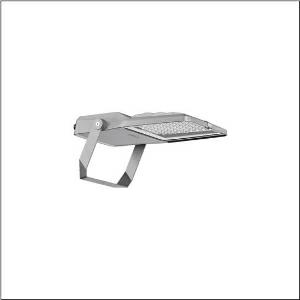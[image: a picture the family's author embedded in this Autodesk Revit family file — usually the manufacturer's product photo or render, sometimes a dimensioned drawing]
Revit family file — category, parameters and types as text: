
# Revit family: floodlight_fl_21_mini___pl64_5xa7772c2e1a_4ebe
name_source: partatom
category: Lighting Fixtures
units: mm (PartAtom-declared; Revit-internal decimal feet)

## family parameters
Cut with Voids When Loaded = No
Host = Face
Light Source = No
Part Type = Normal
Room Calculation Point = No
Round Connector Dimension = Use Diameter
Shared = No

## types (1)
- --- (1 x LED, 11790 lm, 87.2 W, 3000K)
    Apparent Load = 87 VA
    CIE Flux Codes = 28 80 98 100 100
    Color Rendering = 70
    Color Temperature = 3000K
    Default Elevation = 1800 mm
    Description = Floodlight FL 21 mini, floodlight, primary light control with lens, of PMMA, primary optical cover: protective disc, of toughened safety glass, transparent, light distribution: PL64, light emission: direct distribution, installation type: surface-mounted, LED, High Power LED, rated luminous flux: 11.790lm, luminous efficacy: 135lm/W, light colour: 730, colour temperature: 3000K, control gear: ECG iQ, control: Street-Remote, Auto-Match, Temp-Guard, Night-Set, Smart-Wire, Desk-Remote (wireless, voltage-free reading and setting of iQ features in the workshop via application-optimized NFC function/RFID function), optimised constant luminous flux control (CLO 2.0), with terminal, 6-pole, mains connection: 220..240V, AC, 50/60Hz, start of lifetime: 87W, end of lifetime: 92W, reduction: 40W, luminaire housing, of diecast aluminium, powder-coated, Siteco® metallic grey (DB 702S), corrosivity category C5 according to DIN EN ISO 12944, mounting bracket, of steel, galvanised, powder-coated, Siteco® metallic grey (DB 702S), protection rating (complete): IP66, insulation class (complete): insulation class II (safety insulation), certification: CE, ENEC, VDE, protection symbol: D, impact resistance: IK08, permissible operating ambient temperature: -40..+40°C, permissible operating ambient temperature for outdoor applications: -40..+50°C, standard: DIN EN 12944, packaging unit: 1 piece

Light Distribution: PL64
    Height = 70 mm
    Lamp = 1 x LED
    Lamp Light Flux = 11790 lm
    Lamp Power = 87.2 W
    Lamp count = 1
    Length = 485 mm
    Luminous efficacy = 135 lm/W
    Manufacturer = Siteco
    ModVariant = No
    Model = 5XA7772C2E1A
    Number of Poles = 1
    OnlyDefault = Yes
    Power Factor = 1
    Product Name = Floodlight FL 21 mini | PL64
    Product group = floodlight | pylon top
    ProductGroupID = 6101
    Protection Class = Protection class II
    Protection Degree = IP 66
    RLX_Detail_Level = 1
    RlxData = <blob elided: 96265 chars, md5=31dd94d5>
    Socket = socket
    Standby Power = 0 W
    System Light Flux = 11790 lm
    System Power = 87 W
    Type Comments = factory setting: luminous flux: 100 % | dim-lin: 254 | 456 mA
    Type Image = l_1006845.jpg
    URL = http://relux.com
    VarID = @adj_077485
    Voltage = 0 V
    Weight = 0.00 kg
    Width = 337 mm

## geometry (parser evidence)
native form markers: Blend x4, Sweep x14
no freeform markers — native parametric forms only
